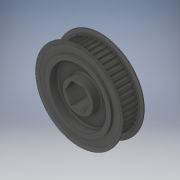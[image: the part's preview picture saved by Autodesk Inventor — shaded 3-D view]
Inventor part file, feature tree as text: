
AUTODESK INVENTOR PART (.ipt)
format: ipt  version: 2017 (Build 210142000, 142)  size: 563,200 bytes
history: native  units: in
note: dims shown in document units (in); Inventor stores cm internally (conversion verified against a paired STEP export)
features: fillet x1
ambient origin geometry x8: Origin, YZ Plane, XZ Plane, XY Plane, X Axis, Y Axis, Z Axis, Center Point
bodies: Solid1 (feature_tree)
feature tree (1):
  fillet  "Fillet1"  [1 undecoded]
note: 1 required parameter value undecoded (feature->parameter linkage not recoverable at this tier; creation-order binding heuristic only, values carry confidence <= 0.55)
